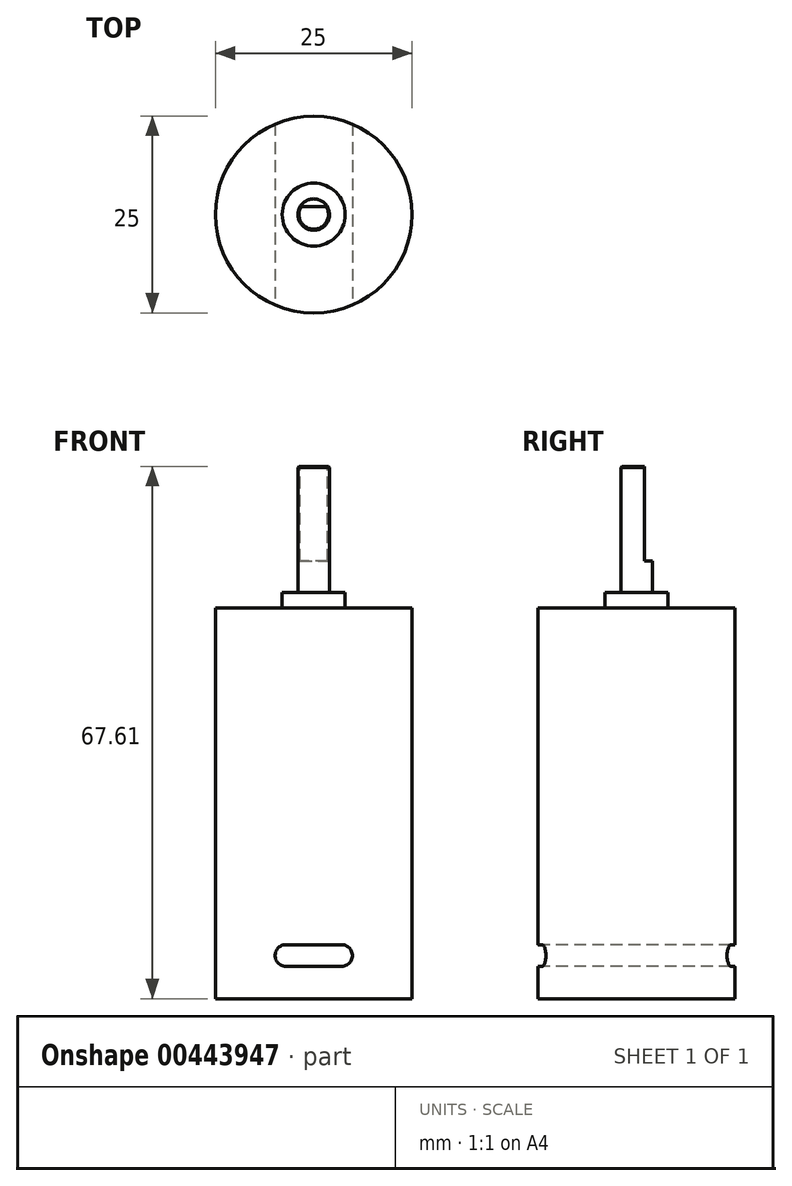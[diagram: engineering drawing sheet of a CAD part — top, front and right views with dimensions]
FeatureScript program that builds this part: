
annotation { "Feature Type Name" : "Feature", "Feature Type Description" : "" }
export const myFeature = defineFeature(function(context is Context, id is Id, definition is map)
    precondition{}
    {
        {
            var Q0;
            Q0=qCreatedBy(makeId("Right.planeOp"),FACE);
            var sketch = newSketch(context, id + "F0", { "sketchPlane" : qUnion([Q0])});
            skLineSegment(sketch, "E0", {"start": v(0, 0) * mm, "end": v(12.5, 0) * mm});
            skLineSegment(sketch, "E1", {"start": v(12.5, 0) * mm, "end": v(12.5, 49.6) * mm});
            skLineSegment(sketch, "E2", {"start": v(12.5, 49.6) * mm, "end": v(4, 49.6) * mm});
            skLineSegment(sketch, "E3", {"start": v(4, 49.6) * mm, "end": v(4, 51.61) * mm});
            skLineSegment(sketch, "E4", {"start": v(4, 51.61) * mm, "end": v(2, 51.61) * mm});
            skLineSegment(sketch, "E5", {"start": v(2, 51.61) * mm, "end": v(2, 67.61) * mm});
            skLineSegment(sketch, "E6", {"start": v(2, 67.61) * mm, "end": v(0, 67.61) * mm});
            skLineSegment(sketch, "E7", {"start": v(0, 67.6) * mm, "end": v(0, 0) * mm});
            skSolve(sketch);
        }
        {
            var Q0;
            Q0=makeQuery(id+"F0.imprint","IMPRINT",FACE,{"disambiguationData":[TD([[makeQuery(id+"F0.imprint","IMPRINT",EDGE,{"derivedFrom":sQuery(id+"F0.wireOp",EDGE,"E0")}),1.0]])]});
            var Q1;
            Q1=sQuery(id+"F0.wireOp",EDGE,"E7");
            revolve(context, id + "F1", {"entities" : qUnion([Q0]), "axis" : qUnion([Q1]), "revolveType" : RevolveType.FULL});
        }
        {
            var Q0;
            Q0=makeQuery(id+"F1.opRevolve","SWEPT_FACE",FACE,{"disambiguationData":[OSD([sQuery(id+"F0.wireOp",EDGE,"E6")])]});
            var sketch = newSketch(context, id + "F2", { "sketchPlane" : qUnion([Q0])});
            skLineSegment(sketch, "E8.bottom", {"start": v(-1.73, 1) * mm, "end": v(1.73, 1) * mm});
            skLineSegment(sketch, "E8.top", {"start": v(-1.73, 2) * mm, "end": v(1.73, 2) * mm});
            skLineSegment(sketch, "E8.left", {"start": v(-1.73, 1) * mm, "end": v(-1.73, 2) * mm});
            skLineSegment(sketch, "E8.right", {"start": v(1.73, 1) * mm, "end": v(1.73, 2) * mm});
            skSolve(sketch);
        }
        {
            var Q0;
            Q0=qSketchRegion(id+"F2",true);
            extrude(context, id + "F3", {"entities" : qUnion([Q0]), "operationType" : NewBodyOperationType.REMOVE, "oppositeDirection" : true, "depth" : 12 * mm});
        }
        {
            var Q0;
            Q0=makeQuery(id+"F1.opRevolve","SWEPT_EDGE",EDGE,{"disambiguationData":[OSD([sQuery(id+"F0.wireOp",EDGE,"E5"),sQuery(id+"F0.wireOp",EDGE,"E6")])]});
            chamfer(context, id + "F4", {"entities" : qUnion([Q0]), "width" : 0.13 * mm, "tangentPropagation" : true});
        }
        {
            var Q0;
            Q0=qCreatedBy(makeId("Front.planeOp"),FACE);
            var sketch = newSketch(context, id + "F5", { "sketchPlane" : qUnion([Q0])});
            skLineSegment(sketch, "E9.bottom", {"start": v(-3.52, 6.86) * mm, "end": v(3.52, 6.86) * mm});
            skLineSegment(sketch, "E9.top", {"start": v(-3.52, 4.09) * mm, "end": v(3.52, 4.09) * mm});
            skLineSegment(sketch, "E9.left", {"start": v(-3.52, 6.86) * mm, "end": v(-3.52, 4.09) * mm});
            skLineSegment(sketch, "E9.right", {"start": v(3.52, 6.86) * mm, "end": v(3.52, 4.09) * mm});
            skCircle(sketch, "E10", {"center": v(-3.52, 5.47) * mm, "radius": 1.38 * mm});
            skCircle(sketch, "E11", {"center": v(3.52, 5.47) * mm, "radius": 1.38 * mm});
            skLineSegment(sketch, "E12", {"start": v(0, -0.48) * mm, "end": v(0, 4.09) * mm, "construction": true});
            skSolve(sketch);
        }
        {
            var Q0;
            Q0=qSketchRegion(id+"F5",true);
            extrude(context, id + "F6", {"entities" : qUnion([Q0]), "operationType" : NewBodyOperationType.REMOVE, "endBound" : BoundingType.SYMMETRIC, "oppositeDirection" : true, "depth" : 152.4 * mm});
        }
    });
